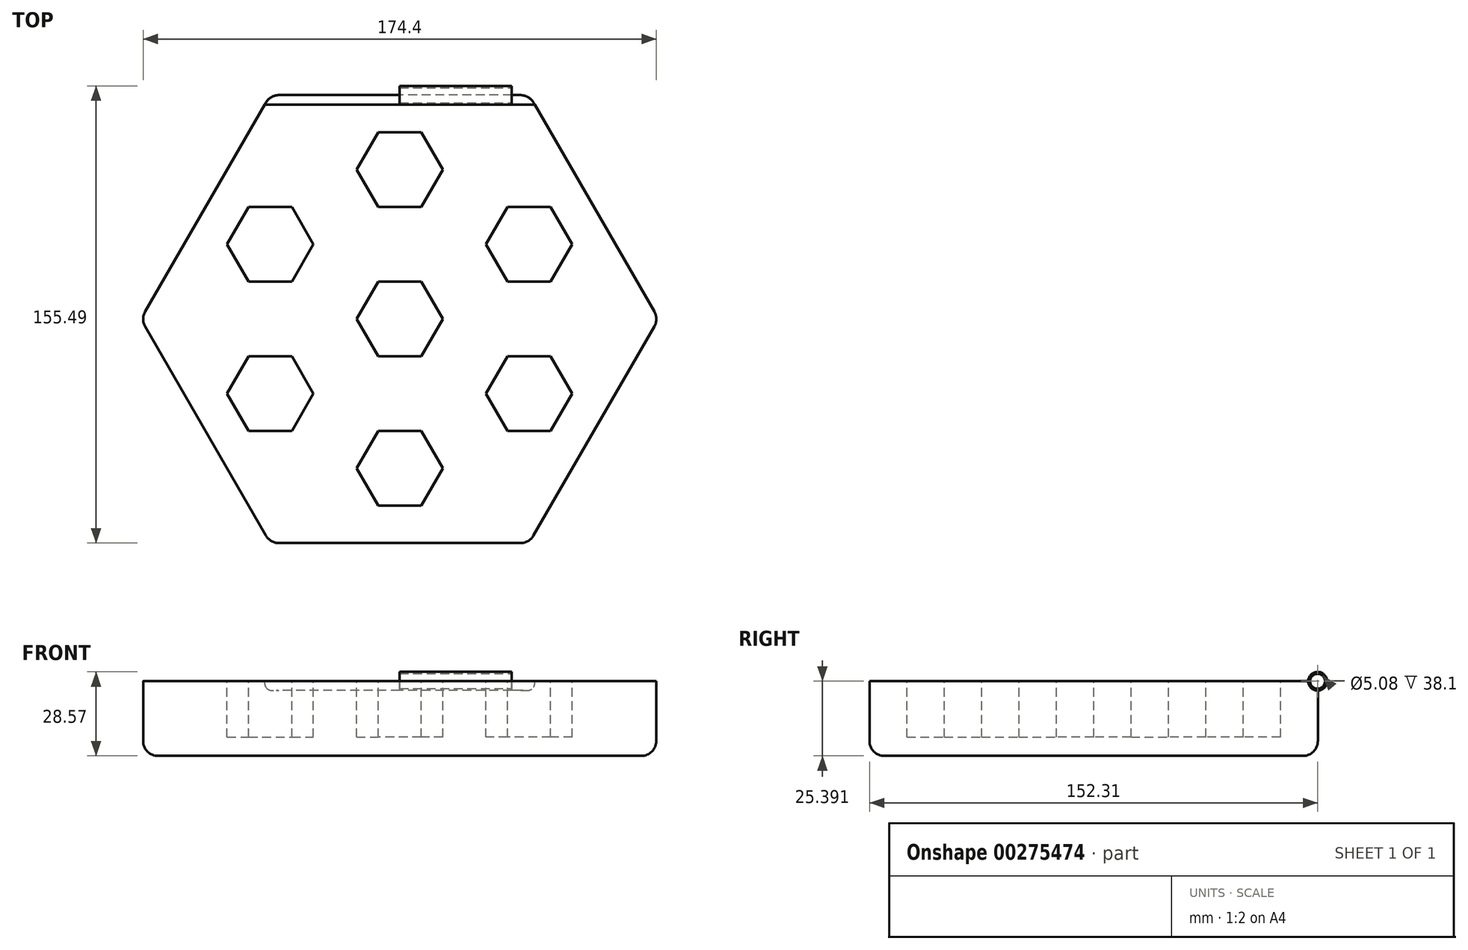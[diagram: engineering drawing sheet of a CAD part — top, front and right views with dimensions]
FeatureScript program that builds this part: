
annotation { "Feature Type Name" : "Feature", "Feature Type Description" : "" }
export const myFeature = defineFeature(function(context is Context, id is Id, definition is map)
    precondition{}
    {
        {
            var Q0;
            Q0=qCreatedBy(makeId("Top.planeOp"),FACE);
            var sketch = newSketch(context, id + "F0", { "sketchPlane" : qUnion([Q0])});
            skCircle(sketch, "E0.cCircle", {"center": v(0, 0) * mm, "radius": 76.2 * mm, "construction": true});
            skLineSegment(sketch, "E0.0", {"start": v(44, -76.2) * mm, "end": v(-44, -76.2) * mm});
            skLineSegment(sketch, "E0.1", {"start": v(-44, -76.2) * mm, "end": v(-87.99, 0) * mm});
            skLineSegment(sketch, "E0.2", {"start": v(-87.99, 0) * mm, "end": v(-44, 76.2) * mm});
            skLineSegment(sketch, "E0.3", {"start": v(-44, 76.2) * mm, "end": v(44, 76.2) * mm});
            skLineSegment(sketch, "E0.4", {"start": v(44, 76.2) * mm, "end": v(87.99, 0) * mm});
            skLineSegment(sketch, "E0.5", {"start": v(87.99, 0) * mm, "end": v(44, -76.2) * mm});
            skPoint(sketch, "E0.0.midPoint", {"position": v(0, -76.2) * mm});
            skSolve(sketch);
        }
        {
            var Q0;
            Q0 = qSketchRegion(id + "F0", true);
            extrude(context, id + "F1", {"entities" : qUnion([Q0]), "depth" : 25.4 * mm});
        }
        {
            var Q0;
            Q0=makeQuery(id+"F1.opExtrude","CAP_FACE",FACE,{"disambiguationData":[OSD([sQuery(id+"F0.wireOp",EDGE,"E0.0"),sQuery(id+"F0.wireOp",EDGE,"E0.1"),sQuery(id+"F0.wireOp",EDGE,"E0.2"),sQuery(id+"F0.wireOp",EDGE,"E0.3"),sQuery(id+"F0.wireOp",EDGE,"E0.4"),sQuery(id+"F0.wireOp",EDGE,"E0.5")])],"isStart":false});
            var sketch = newSketch(context, id + "F2", { "sketchPlane" : qUnion([Q0])});
            skCircle(sketch, "E1.cCircle", {"center": v(0, 0) * mm, "radius": 12.7 * mm, "construction": true});
            skLineSegment(sketch, "E1.0", {"start": v(7.33, -12.7) * mm, "end": v(-7.33, -12.7) * mm});
            skLineSegment(sketch, "E1.1", {"start": v(-7.33, -12.7) * mm, "end": v(-14.66, 0) * mm});
            skLineSegment(sketch, "E1.2", {"start": v(-14.66, 0) * mm, "end": v(-7.33, 12.7) * mm});
            skLineSegment(sketch, "E1.3", {"start": v(-7.33, 12.7) * mm, "end": v(7.33, 12.7) * mm});
            skLineSegment(sketch, "E1.4", {"start": v(7.33, 12.7) * mm, "end": v(14.66, 0) * mm});
            skLineSegment(sketch, "E1.5", {"start": v(14.66, 0) * mm, "end": v(7.33, -12.7) * mm});
            skPoint(sketch, "E1.0.midPoint", {"position": v(0, -12.7) * mm});
            skCircle(sketch, "E2.cCircle", {"center": v(0, 50.8) * mm, "radius": 12.7 * mm, "construction": true});
            skLineSegment(sketch, "E2.0", {"start": v(7.33, 38.1) * mm, "end": v(-7.33, 38.1) * mm});
            skLineSegment(sketch, "E2.1", {"start": v(-7.33, 38.1) * mm, "end": v(-14.66, 50.8) * mm});
            skLineSegment(sketch, "E2.2", {"start": v(-14.66, 50.8) * mm, "end": v(-7.33, 63.5) * mm});
            skLineSegment(sketch, "E2.3", {"start": v(-7.33, 63.5) * mm, "end": v(7.33, 63.5) * mm});
            skLineSegment(sketch, "E2.4", {"start": v(7.33, 63.5) * mm, "end": v(14.66, 50.8) * mm});
            skLineSegment(sketch, "E2.5", {"start": v(14.66, 50.8) * mm, "end": v(7.33, 38.1) * mm});
            skPoint(sketch, "E2.0.midPoint", {"position": v(0, 38.1) * mm});
            skLineSegment(sketch, "E3.1.0", {"start": v(-36.66, 38.1) * mm, "end": v(-29.33, 25.4) * mm});
            skLineSegment(sketch, "E3.1.1", {"start": v(-51.33, 38.1) * mm, "end": v(-36.66, 38.1) * mm});
            skLineSegment(sketch, "E3.1.2", {"start": v(-58.66, 25.4) * mm, "end": v(-51.33, 38.1) * mm});
            skLineSegment(sketch, "E3.1.3", {"start": v(-51.33, 12.7) * mm, "end": v(-58.66, 25.4) * mm});
            skLineSegment(sketch, "E3.1.4", {"start": v(-36.66, 12.7) * mm, "end": v(-51.33, 12.7) * mm});
            skLineSegment(sketch, "E3.1.5", {"start": v(-29.33, 25.4) * mm, "end": v(-36.66, 12.7) * mm});
            skLineSegment(sketch, "E3.2.0", {"start": v(-51.33, -12.7) * mm, "end": v(-36.66, -12.7) * mm});
            skLineSegment(sketch, "E3.2.1", {"start": v(-58.66, -25.4) * mm, "end": v(-51.33, -12.7) * mm});
            skLineSegment(sketch, "E3.2.2", {"start": v(-51.33, -38.1) * mm, "end": v(-58.66, -25.4) * mm});
            skLineSegment(sketch, "E3.2.3", {"start": v(-36.66, -38.1) * mm, "end": v(-51.33, -38.1) * mm});
            skLineSegment(sketch, "E3.2.4", {"start": v(-29.33, -25.4) * mm, "end": v(-36.66, -38.1) * mm});
            skLineSegment(sketch, "E3.2.5", {"start": v(-36.66, -12.7) * mm, "end": v(-29.33, -25.4) * mm});
            skLineSegment(sketch, "E3.3.0", {"start": v(-14.66, -50.8) * mm, "end": v(-7.33, -38.1) * mm});
            skLineSegment(sketch, "E3.3.1", {"start": v(-7.33, -63.5) * mm, "end": v(-14.66, -50.8) * mm});
            skLineSegment(sketch, "E3.3.2", {"start": v(7.33, -63.5) * mm, "end": v(-7.33, -63.5) * mm});
            skLineSegment(sketch, "E3.3.3", {"start": v(14.66, -50.8) * mm, "end": v(7.33, -63.5) * mm});
            skLineSegment(sketch, "E3.3.4", {"start": v(7.33, -38.1) * mm, "end": v(14.66, -50.8) * mm});
            skLineSegment(sketch, "E3.3.5", {"start": v(-7.33, -38.1) * mm, "end": v(7.33, -38.1) * mm});
            skLineSegment(sketch, "E3.4.0", {"start": v(36.66, -38.1) * mm, "end": v(29.33, -25.4) * mm});
            skLineSegment(sketch, "E3.4.1", {"start": v(51.33, -38.1) * mm, "end": v(36.66, -38.1) * mm});
            skLineSegment(sketch, "E3.4.2", {"start": v(58.66, -25.4) * mm, "end": v(51.33, -38.1) * mm});
            skLineSegment(sketch, "E3.4.3", {"start": v(51.33, -12.7) * mm, "end": v(58.66, -25.4) * mm});
            skLineSegment(sketch, "E3.4.4", {"start": v(36.66, -12.7) * mm, "end": v(51.33, -12.7) * mm});
            skLineSegment(sketch, "E3.4.5", {"start": v(29.33, -25.4) * mm, "end": v(36.66, -12.7) * mm});
            skLineSegment(sketch, "E3.5.0", {"start": v(51.33, 12.7) * mm, "end": v(36.66, 12.7) * mm});
            skLineSegment(sketch, "E3.5.1", {"start": v(58.66, 25.4) * mm, "end": v(51.33, 12.7) * mm});
            skLineSegment(sketch, "E3.5.2", {"start": v(51.33, 38.1) * mm, "end": v(58.66, 25.4) * mm});
            skLineSegment(sketch, "E3.5.3", {"start": v(36.66, 38.1) * mm, "end": v(51.33, 38.1) * mm});
            skLineSegment(sketch, "E3.5.4", {"start": v(29.33, 25.4) * mm, "end": v(36.66, 38.1) * mm});
            skLineSegment(sketch, "E3.5.5", {"start": v(36.66, 12.7) * mm, "end": v(29.33, 25.4) * mm});
            skSolve(sketch);
        }
        {
            var Q0;
            Q0 = qSketchRegion(id + "F2", true);
            extrude(context, id + "F3", {"entities" : qUnion([Q0]), "operationType" : NewBodyOperationType.REMOVE, "oppositeDirection" : true, "depth" : 19.05 * mm});
        }
        {
            var Q0;
            Q0=makeQuery(id+"F1.opExtrude","CAP_FACE",FACE,{"disambiguationData":[OSD([sQuery(id+"F0.wireOp",EDGE,"E0.0"),sQuery(id+"F0.wireOp",EDGE,"E0.1"),sQuery(id+"F0.wireOp",EDGE,"E0.2"),sQuery(id+"F0.wireOp",EDGE,"E0.3"),sQuery(id+"F0.wireOp",EDGE,"E0.4"),sQuery(id+"F0.wireOp",EDGE,"E0.5")])],"isStart":true});
            var Q1;
            Q1=makeQuery(id+"F1.opExtrude","SWEPT_EDGE",EDGE,{"disambiguationData":[OSD([sQuery(id+"F0.wireOp",EDGE,"E0.0"),sQuery(id+"F0.wireOp",EDGE,"E0.5")])]});
            var Q2;
            Q2=makeQuery(id+"F1.opExtrude","SWEPT_EDGE",EDGE,{"disambiguationData":[OSD([sQuery(id+"F0.wireOp",EDGE,"E0.4"),sQuery(id+"F0.wireOp",EDGE,"E0.5")])]});
            var Q3;
            Q3=makeQuery(id+"F1.opExtrude","SWEPT_EDGE",EDGE,{"disambiguationData":[OSD([sQuery(id+"F0.wireOp",EDGE,"E0.0"),sQuery(id+"F0.wireOp",EDGE,"E0.1")])]});
            var Q4;
            Q4=makeQuery(id+"F1.opExtrude","SWEPT_EDGE",EDGE,{"disambiguationData":[OSD([sQuery(id+"F0.wireOp",EDGE,"E0.2"),sQuery(id+"F0.wireOp",EDGE,"E0.3")])]});
            var Q5;
            Q5=makeQuery(id+"F1.opExtrude","SWEPT_EDGE",EDGE,{"disambiguationData":[OSD([sQuery(id+"F0.wireOp",EDGE,"E0.3"),sQuery(id+"F0.wireOp",EDGE,"E0.4")])]});
            var Q6;
            Q6=makeQuery(id+"F1.opExtrude","SWEPT_EDGE",EDGE,{"disambiguationData":[OSD([sQuery(id+"F0.wireOp",EDGE,"E0.1"),sQuery(id+"F0.wireOp",EDGE,"E0.2")])]});
            fillet(context, id + "F4", {"entities" : qUnion([Q0, Q1, Q2, Q3, Q4, Q5, Q6]), "radius" : 5.08 * mm, "tangentPropagation" : true, "allowEdgeOverflow" : false});
        }
        {
            var Q0;
            Q0=qCreatedBy(makeId("Right.planeOp"),FACE);
            var sketch = newSketch(context, id + "F5", { "sketchPlane" : qUnion([Q0])});
            skCircle(sketch, "E4", {"center": v(76.11, 25.4) * mm, "radius": 3.18 * mm});
            skSolve(sketch);
        }
        {
            var Q0;
            Q0 = qSketchRegion(id + "F5", true);
            extrude(context, id + "F6", {"entities" : qUnion([Q0]), "operationType" : NewBodyOperationType.REMOVE, "endBound" : BoundingType.THROUGH_ALL, "depth" : 25.4 * mm, "hasSecondDirection" : true, "secondDirectionBound" : BoundingType.THROUGH_ALL, "secondDirectionOppositeDirection" : true, "secondDirectionDepth" : 25.4 * mm});
        }
        {
            var Q0;
            Q0=makeQuery(id+"F5.imprint","IMPRINT",FACE,{"disambiguationData":[TD([[makeQuery(id+"F5.imprint","IMPRINT",EDGE,{"derivedFrom":sQuery(id+"F5.wireOp",EDGE,"E4")}),1.0]])]});
            extrude(context, id + "F7", {"entities" : qUnion([Q0]), "operationType" : NewBodyOperationType.ADD, "depth" : 38.1 * mm});
        }
        {
            var Q0;
            Q0=makeQuery(id+"F7.opExtrude","CAP_FACE",FACE,{"disambiguationData":[OSD([sQuery(id+"F5.wireOp",EDGE,"E4")])],"isStart":false});
            var sketch = newSketch(context, id + "F8", { "sketchPlane" : qUnion([Q0])});
            skCircle(sketch, "E5", {"center": v(76.11, 25.4) * mm, "radius": 2.54 * mm});
            skSolve(sketch);
        }
        {
            var Q0;
            Q0 = qSketchRegion(id + "F8", true);
            extrude(context, id + "F9", {"entities" : qUnion([Q0]), "operationType" : NewBodyOperationType.REMOVE, "endBound" : BoundingType.THROUGH_ALL, "oppositeDirection" : true, "depth" : 25.4 * mm});
        }
    });
